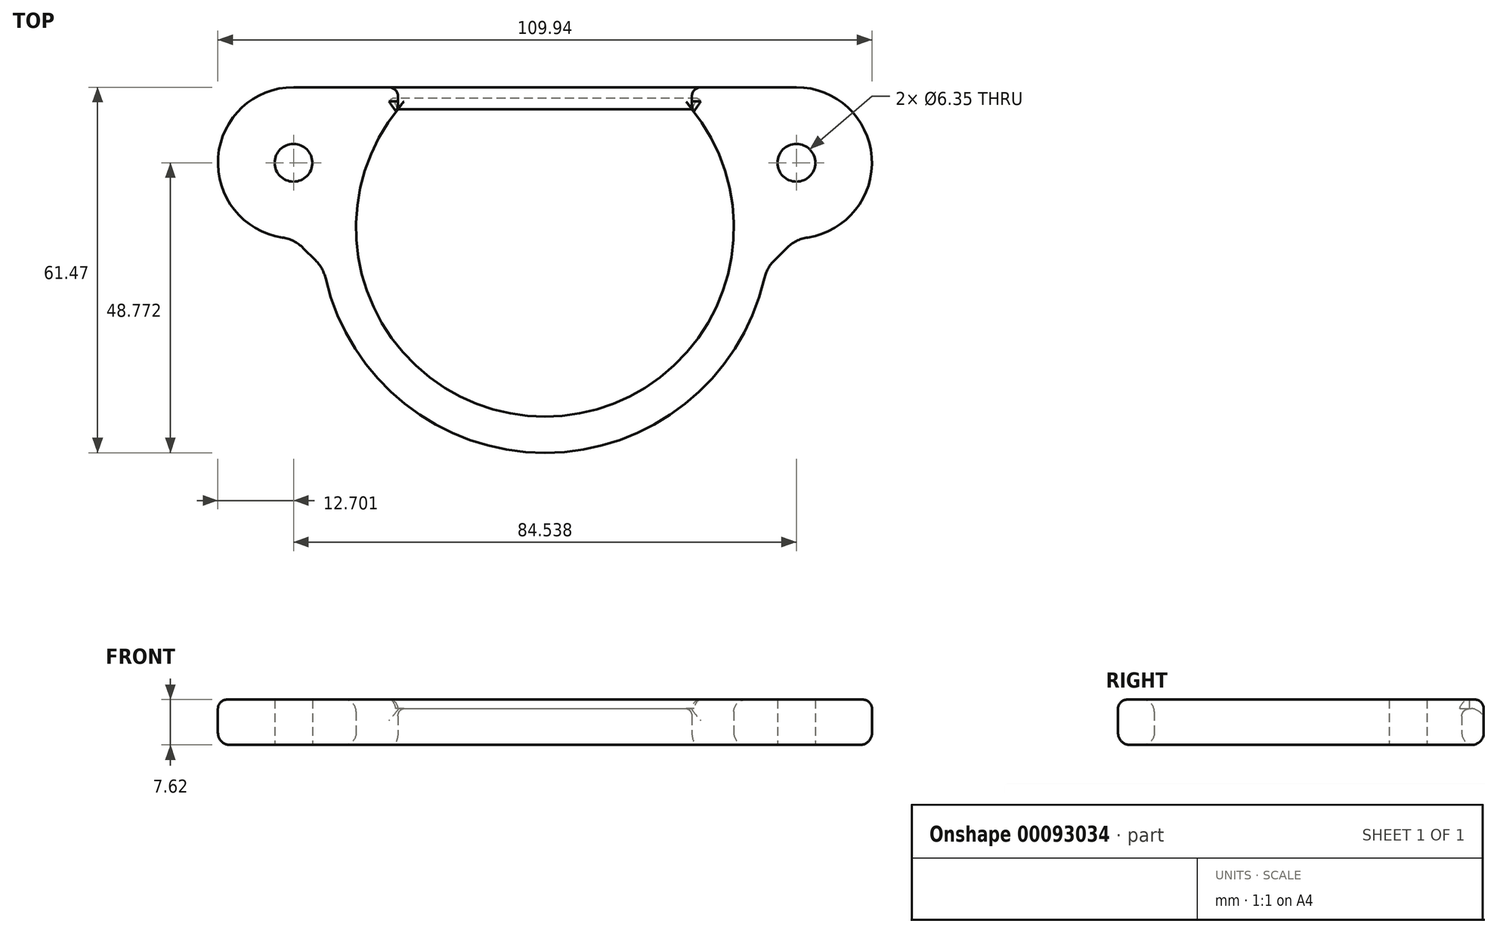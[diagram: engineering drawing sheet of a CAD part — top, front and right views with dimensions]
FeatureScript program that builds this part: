
annotation { "Feature Type Name" : "Feature", "Feature Type Description" : "" }
export const myFeature = defineFeature(function(context is Context, id is Id, definition is map)
    precondition{}
    {
        {
            var Q0;
            Q0=qCreatedBy(makeId("Top.planeOp"),FACE);
            var sketch = newSketch(context, id + "F0", { "sketchPlane" : qUnion([Q0])});
            skArc(sketch, "E0", {"start": v(-24.7, 19.94) * mm, "mid": v(0, -31.75) * mm, "end": v(24.7, 19.94) * mm});
            skArc(sketch, "E1", {"start": v(-36.87, -8.54) * mm, "mid": v(0, -37.85) * mm, "end": v(36.87, -8.54) * mm});
            skPoint(sketch, "E2", {"position": v(0, 23.62) * mm});
            skLineSegment(sketch, "E3", {"start": v(-29.57, 23.62) * mm, "end": v(29.57, 23.62) * mm});
            skPoint(sketch, "E4", {"position": v(0, 19.94) * mm});
            skLineSegment(sketch, "E5", {"start": v(-24.7, 19.94) * mm, "end": v(24.7, 19.94) * mm});
            skPoint(sketch, "E6.orphan", {"position": v(-32.17, 19.94) * mm});
            skLineSegment(sketch, "E7", {"start": v(-24.7, 19.94) * mm, "end": v(-24.7, 23.62) * mm});
            skLineSegment(sketch, "E8", {"start": v(24.7, 19.94) * mm, "end": v(24.7, 23.62) * mm});
            skLineSegment(sketch, "E9", {"start": v(-29.57, 23.62) * mm, "end": v(-42.27, 23.62) * mm});
            skLineSegment(sketch, "E10", {"start": v(-54.97, 10.92) * mm, "end": v(-54.97, 10.92) * mm});
            skPoint(sketch, "E11.visualSharp", {"position": v(-54.97, 23.62) * mm});
            skArc(sketch, "E11.filletArc", {"start": v(-42.27, 23.62) * mm, "mid": v(-51.25, 19.9) * mm, "end": v(-54.97, 10.92) * mm});
            skPoint(sketch, "E12.visualSharp", {"position": v(-54.97, -1.78) * mm});
            skArc(sketch, "E12.filletArc", {"start": v(-54.97, 10.92) * mm, "mid": v(-51.9, 2.64) * mm, "end": v(-44.16, -1.64) * mm});
            skLineSegment(sketch, "E13", {"start": v(-40.62, -3.42) * mm, "end": v(-38.57, -5.48) * mm});
            skPoint(sketch, "E14.visualSharp", {"position": v(-42.27, -1.78) * mm});
            skArc(sketch, "E14.filletArc", {"start": v(-40.62, -3.42) * mm, "mid": v(-42.25, -2.25) * mm, "end": v(-44.16, -1.64) * mm});
            skArc(sketch, "E15.filletArc", {"start": v(-36.87, -8.54) * mm, "mid": v(-37.5, -6.9) * mm, "end": v(-38.57, -5.48) * mm});
            skCircle(sketch, "E16", {"center": v(-42.27, 10.92) * mm, "radius": 3.18 * mm});
            skLineSegment(sketch, "E17", {"start": v(29.57, 23.62) * mm, "end": v(42.27, 23.62) * mm});
            skLineSegment(sketch, "E18", {"start": v(54.97, 10.92) * mm, "end": v(54.97, 10.92) * mm});
            skPoint(sketch, "E19.visualSharp", {"position": v(54.97, -1.78) * mm});
            skArc(sketch, "E19.filletArc", {"start": v(44.16, -1.64) * mm, "mid": v(51.9, 2.64) * mm, "end": v(54.97, 10.92) * mm});
            skPoint(sketch, "E20.visualSharp", {"position": v(54.97, 23.62) * mm});
            skArc(sketch, "E20.filletArc", {"start": v(54.97, 10.92) * mm, "mid": v(51.25, 19.9) * mm, "end": v(42.27, 23.62) * mm});
            skLineSegment(sketch, "E21", {"start": v(40.62, -3.42) * mm, "end": v(38.57, -5.48) * mm});
            skPoint(sketch, "E22.visualSharp", {"position": v(42.27, -1.78) * mm});
            skArc(sketch, "E22.filletArc", {"start": v(44.16, -1.64) * mm, "mid": v(42.25, -2.25) * mm, "end": v(40.62, -3.42) * mm});
            skArc(sketch, "E23.filletArc", {"start": v(38.57, -5.48) * mm, "mid": v(37.5, -6.9) * mm, "end": v(36.87, -8.54) * mm});
            skCircle(sketch, "E24", {"center": v(42.27, 10.92) * mm, "radius": 3.18 * mm});
            skSolve(sketch);
        }
        {
            var Q0;
            Q0=makeQuery(id+"F0.imprint","IMPRINT",FACE,{"disambiguationData":[TD([[makeQuery(id+"F0.imprint","IMPRINT",EDGE,{"derivedFrom":sQuery(id+"F0.wireOp",EDGE,"E5")}),1.0]])]});
            extrude(context, id + "F1", {"entities" : qUnion([Q0]), "depth" : 6.1 * mm});
        }
        {
            var Q0;
            {var subQ0=sQuery(id+"F0.wireOp",EDGE,"siQIgWPf-HaQZ-ZDgq-PbrE-CyyWj0YIvhzH");Q0=makeQuery(id+"F0.imprint","IMPRINT",FACE,{"disambiguationData":[TD([[makeQuery(id+"F0.imprint","IMPRINT",EDGE,{"derivedFrom":subQ0}),-1.0]])]});}
            var Q1;
            Q1=makeQuery(id+"F0.imprint","IMPRINT",FACE,{"disambiguationData":[TD([[makeQuery(id+"F0.imprint","IMPRINT",EDGE,{"derivedFrom":sQuery(id+"F0.wireOp",EDGE,"E0")}),-1.0]])]});
            extrude(context, id + "F2", {"entities" : qUnion([Q0, Q1]), "operationType" : NewBodyOperationType.ADD, "depth" : 7.62 * mm});
        }
        {
            var Q0;
            Q0=makeQuery(id+"F1.opExtrude","CAP_EDGE",EDGE,{"disambiguationData":[OSD([sQuery(id+"F0.wireOp",EDGE,"E3")])],"isStart":false});
            var Q1;
            {var subQ0=sQuery(id+"F0.wireOp",EDGE,"E1");Q1=makeQuery(id+"F1.opExtrude","CAP_EDGE",EDGE,{"disambiguationData":[OSD([subQ0]),TDD([makeQuery(id+"F0.imprint","IMPRINT",EDGE,{"disambiguationData":[TD([[makeQuery(id+"F0.imprint","INTERSECT",VERTEX,{"disambiguationData":[OD(0.0)],"derivedFrom":[subQ0,sQuery(id+"F0.wireOp",EDGE,"E3")]}),-1.0]])],"derivedFrom":subQ0})])],"isStart":false});}
            var Q2;
            {var subQ0=sQuery(id+"F0.wireOp",EDGE,"E1");var subQ1=sQuery(id+"F0.wireOp",EDGE,"E3");Q2=makeQuery(id+"F2.boolean.opBoolean","MERGE",EDGE,{"derivedFrom":[makeQuery(id+"F1.opExtrude","CAP_EDGE",EDGE,{"disambiguationData":[OSD([subQ0]),TDD([makeQuery(id+"F0.imprint","IMPRINT",EDGE,{"disambiguationData":[TD([[makeQuery(id+"F0.imprint","INTERSECT",VERTEX,{"disambiguationData":[OD(0.0)],"derivedFrom":[subQ0,subQ1]}),-1.0]])],"derivedFrom":subQ0})])],"isStart":true}),makeQuery(id+"F1.opExtrude","CAP_EDGE",EDGE,{"disambiguationData":[OSD([subQ0]),TDD([makeQuery(id+"F0.imprint","IMPRINT",EDGE,{"disambiguationData":[TD([[makeQuery(id+"F0.imprint","INTERSECT",VERTEX,{"disambiguationData":[OD(1.0)],"derivedFrom":[subQ0,subQ1]}),1.0]])],"derivedFrom":subQ0})])],"isStart":true}),makeQuery(id+"F2.opExtrude","CAP_EDGE",EDGE,{"disambiguationData":[OSD([subQ0])],"isStart":true})]});}
            var Q3;
            {var subQ0=sQuery(id+"F0.wireOp",EDGE,"E0");var subQ1=sQuery(id+"F0.wireOp",EDGE,"E5");Q3=makeQuery(id+"F2.boolean.opBoolean","MERGE",EDGE,{"derivedFrom":[makeQuery(id+"F1.opExtrude","CAP_EDGE",EDGE,{"disambiguationData":[OSD([subQ0]),TDD([makeQuery(id+"F0.imprint","IMPRINT",EDGE,{"disambiguationData":[TD([[makeQuery(id+"F0.imprint","INTERSECT",VERTEX,{"disambiguationData":[OD(0.0)],"derivedFrom":[subQ0,subQ1]}),-1.0]])],"derivedFrom":subQ0})])],"isStart":true}),makeQuery(id+"F1.opExtrude","CAP_EDGE",EDGE,{"disambiguationData":[OSD([subQ0]),TDD([makeQuery(id+"F0.imprint","IMPRINT",EDGE,{"disambiguationData":[TD([[makeQuery(id+"F0.imprint","INTERSECT",VERTEX,{"disambiguationData":[OD(1.0)],"derivedFrom":[subQ0,subQ1]}),1.0]])],"derivedFrom":subQ0})])],"isStart":true}),makeQuery(id+"F2.opExtrude","CAP_EDGE",EDGE,{"disambiguationData":[OSD([subQ0])],"isStart":true})]});}
            var Q4;
            Q4=makeQuery(id+"F2.opExtrude","CAP_EDGE",EDGE,{"disambiguationData":[OSD([sQuery(id+"F0.wireOp",EDGE,"E0")])],"isStart":false});
            var Q5;
            {var subQ0=sQuery(id+"F0.wireOp",EDGE,"E1");Q5=makeQuery(id+"F1.opExtrude","CAP_EDGE",EDGE,{"disambiguationData":[OSD([subQ0]),TDD([makeQuery(id+"F0.imprint","IMPRINT",EDGE,{"disambiguationData":[TD([[makeQuery(id+"F0.imprint","INTERSECT",VERTEX,{"disambiguationData":[OD(1.0)],"derivedFrom":[subQ0,sQuery(id+"F0.wireOp",EDGE,"E3")]}),1.0]])],"derivedFrom":subQ0})])],"isStart":false});}
            var Q6;
            {var subQ0=sQuery(id+"F0.wireOp",EDGE,"E0");Q6=makeQuery(id+"F1.opExtrude","CAP_EDGE",EDGE,{"disambiguationData":[OSD([subQ0]),TDD([makeQuery(id+"F0.imprint","IMPRINT",EDGE,{"disambiguationData":[TD([[makeQuery(id+"F0.imprint","INTERSECT",VERTEX,{"disambiguationData":[OD(1.0)],"derivedFrom":[subQ0,sQuery(id+"F0.wireOp",EDGE,"E5")]}),1.0]])],"derivedFrom":subQ0})])],"isStart":false});}
            var Q7;
            {var subQ0=sQuery(id+"F0.wireOp",EDGE,"E0");Q7=makeQuery(id+"F1.opExtrude","CAP_EDGE",EDGE,{"disambiguationData":[OSD([subQ0]),TDD([makeQuery(id+"F0.imprint","IMPRINT",EDGE,{"disambiguationData":[TD([[makeQuery(id+"F0.imprint","INTERSECT",VERTEX,{"disambiguationData":[OD(0.0)],"derivedFrom":[subQ0,sQuery(id+"F0.wireOp",EDGE,"E5")]}),-1.0]])],"derivedFrom":subQ0})])],"isStart":false});}
            var Q8;
            Q8=makeQuery(id+"F2.opExtrude","CAP_EDGE",EDGE,{"disambiguationData":[OSD([sQuery(id+"F0.wireOp",EDGE,"E1")])],"isStart":true});
            var Q9;
            Q9=makeQuery(id+"F2.opExtrude","CAP_EDGE",EDGE,{"disambiguationData":[OSD([sQuery(id+"F0.wireOp",EDGE,"E0")])],"isStart":true});
            var Q10;
            Q10=makeQuery(id+"F1.opExtrude","CAP_EDGE",EDGE,{"disambiguationData":[OSD([sQuery(id+"F0.wireOp",EDGE,"E5")])],"isStart":true});
            var Q11;
            {var subQ0=sQuery(id+"F0.wireOp",EDGE,"E3");var subQ1=sQuery(id+"F0.wireOp",EDGE,"E1");Q11=makeQuery(id+"F2.boolean.opBoolean","MERGE",EDGE,{"derivedFrom":[makeQuery(id+"F1.opExtrude","CAP_EDGE",EDGE,{"disambiguationData":[OSD([subQ0])],"isStart":true}),makeQuery(id+"F2.opExtrude","CAP_EDGE",EDGE,{"disambiguationData":[OSD([subQ0]),TDD([makeQuery(id+"F0.imprint","IMPRINT",EDGE,{"disambiguationData":[TD([[makeQuery(id+"F0.imprint","INTERSECT",VERTEX,{"disambiguationData":[OD(0.0)],"derivedFrom":[subQ1,subQ0]}),-1.0]])],"derivedFrom":subQ0})])],"isStart":true}),makeQuery(id+"F2.opExtrude","CAP_EDGE",EDGE,{"disambiguationData":[OSD([subQ0]),TDD([makeQuery(id+"F0.imprint","IMPRINT",EDGE,{"disambiguationData":[TD([[makeQuery(id+"F0.imprint","INTERSECT",VERTEX,{"disambiguationData":[OD(1.0)],"derivedFrom":[subQ1,subQ0]}),1.0]])],"derivedFrom":subQ0})])],"isStart":true})]});}
            fillet(context, id + "F3", {"entities" : qUnion([Q0, Q1, Q2, Q3, Q4, Q5, Q6, Q7, Q8, Q9, Q10, Q11]), "radius" : 2.03 * mm, "tangentPropagation" : true, "allowEdgeOverflow" : false});
        }
        {
            var Q0;
            Q0=makeQuery(id+"F2.opExtrude","CAP_EDGE",EDGE,{"disambiguationData":[OSD([sQuery(id+"F0.wireOp",EDGE,"E1")])],"isStart":false});
            var Q1;
            {var subQ0=sQuery(id+"F0.wireOp",EDGE,"E3");Q1=makeQuery(id+"F2.opExtrude","CAP_EDGE",EDGE,{"disambiguationData":[OSD([subQ0]),TDD([makeQuery(id+"F0.imprint","IMPRINT",EDGE,{"disambiguationData":[TD([[makeQuery(id+"F0.imprint","INTERSECT",VERTEX,{"disambiguationData":[OD(1.0)],"derivedFrom":[sQuery(id+"F0.wireOp",EDGE,"E1"),subQ0]}),1.0]])],"derivedFrom":subQ0})])],"isStart":false});}
            var Q2;
            {var subQ0=sQuery(id+"F0.wireOp",EDGE,"E3");Q2=makeQuery(id+"F2.opExtrude","CAP_EDGE",EDGE,{"disambiguationData":[OSD([subQ0]),TDD([makeQuery(id+"F0.imprint","IMPRINT",EDGE,{"disambiguationData":[TD([[makeQuery(id+"F0.imprint","INTERSECT",VERTEX,{"disambiguationData":[OD(0.0)],"derivedFrom":[sQuery(id+"F0.wireOp",EDGE,"E1"),subQ0]}),-1.0]])],"derivedFrom":subQ0})])],"isStart":false});}
            var Q3;
            Q3=makeQuery(id+"F3.opFillet","BLEND_EDGE",EDGE,{"blendedFrom":[makeQuery(id+"F2.opExtrude","CAP_EDGE",EDGE,{"disambiguationData":[OSD([sQuery(id+"F0.wireOp",EDGE,"E0")])],"isStart":false}),makeQuery(id+"F2.opExtrude","SWEPT_FACE",FACE,{"disambiguationData":[OSD([sQuery(id+"F0.wireOp",EDGE,"E8")])]})],"blendedInto":[makeQuery(id+"F2.opExtrude","SWEPT_FACE",FACE,{"disambiguationData":[OSD([sQuery(id+"F0.wireOp",EDGE,"E8")])]})]});
            var Q4;
            Q4=makeQuery(id+"F2.opExtrude","SWEPT_EDGE",EDGE,{"disambiguationData":[OSD([sQuery(id+"F0.wireOp",EDGE,"E3"),sQuery(id+"F0.wireOp",EDGE,"E8")])]});
            var Q5;
            Q5=makeQuery(id+"F3.opFillet","BLEND_EDGE",EDGE,{"blendedFrom":[makeQuery(id+"F2.opExtrude","CAP_EDGE",EDGE,{"disambiguationData":[OSD([sQuery(id+"F0.wireOp",EDGE,"E0")])],"isStart":false}),makeQuery(id+"F2.opExtrude","SWEPT_FACE",FACE,{"disambiguationData":[OSD([sQuery(id+"F0.wireOp",EDGE,"E7")])]})],"blendedInto":[makeQuery(id+"F2.opExtrude","SWEPT_FACE",FACE,{"disambiguationData":[OSD([sQuery(id+"F0.wireOp",EDGE,"E7")])]})]});
            var Q6;
            Q6=makeQuery(id+"F2.opExtrude","SWEPT_EDGE",EDGE,{"disambiguationData":[OSD([sQuery(id+"F0.wireOp",EDGE,"E3"),sQuery(id+"F0.wireOp",EDGE,"E7")])]});
            fillet(context, id + "F4", {"entities" : qUnion([Q0, Q1, Q2, Q3, Q4, Q5, Q6]), "radius" : 1.52 * mm, "tangentPropagation" : true, "allowEdgeOverflow" : false});
        }
        {
            var Q0;
            Q0=makeQuery(id+"F1.opExtrude","CAP_EDGE",EDGE,{"disambiguationData":[OSD([sQuery(id+"F0.wireOp",EDGE,"E5")])],"isStart":false});
            fillet(context, id + "F5", {"entities" : qUnion([Q0]), "radius" : 1.27 * mm, "tangentPropagation" : true, "allowEdgeOverflow" : false});
        }
    });
